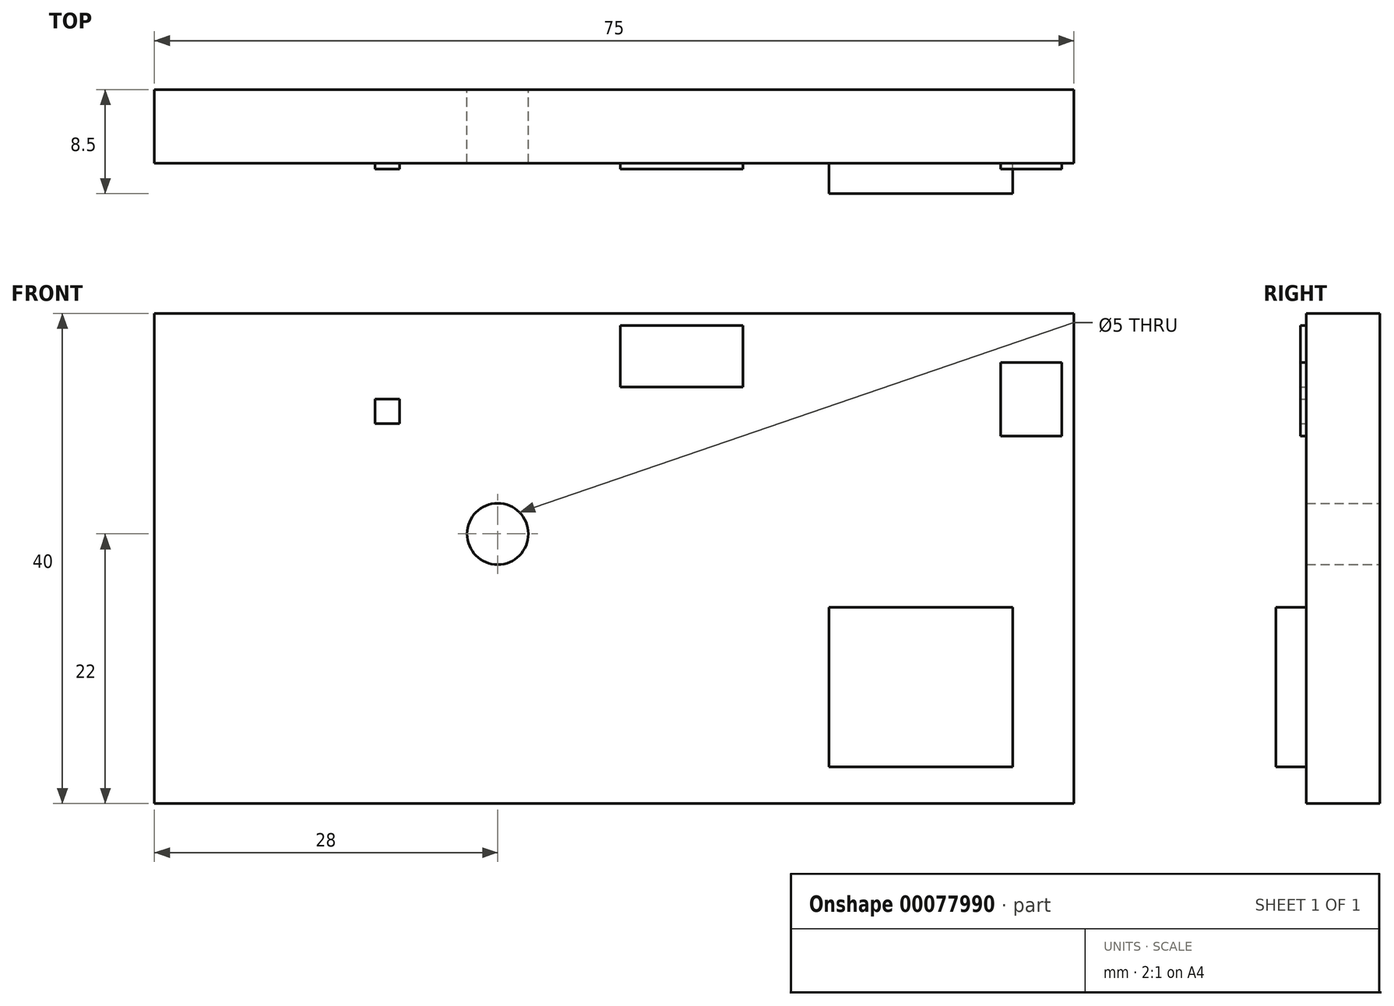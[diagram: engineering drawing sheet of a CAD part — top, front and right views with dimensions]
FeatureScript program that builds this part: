
annotation { "Feature Type Name" : "Feature", "Feature Type Description" : "" }
export const myFeature = defineFeature(function(context is Context, id is Id, definition is map)
    precondition{}
    {
        {
            var Q0;
            Q0=qCreatedBy(makeId("Front.planeOp"),FACE);
            var sketch = newSketch(context, id + "F0", { "sketchPlane" : qUnion([Q0])});
            skLineSegment(sketch, "E0", {"start": v(37.5, -20) * mm, "end": v(-37.5, -20) * mm});
            skLineSegment(sketch, "E1", {"start": v(-37.5, -20) * mm, "end": v(-37.5, 20) * mm});
            skLineSegment(sketch, "E2", {"start": v(-37.5, 20) * mm, "end": v(37.5, 20) * mm});
            skLineSegment(sketch, "E3", {"start": v(37.5, 20) * mm, "end": v(37.5, -20) * mm});
            skPoint(sketch, "E4.endSnap0", {"position": v(-37.5, 0) * mm});
            skCircle(sketch, "E5", {"center": v(-9.5, 2) * mm, "radius": 2.5 * mm});
            skSolve(sketch);
        }
        {
            var Q0;
            Q0=qSketchRegion(id+"F0",true);
            extrude(context, id + "F1", {"entities" : qUnion([Q0]), "depth" : 6 * mm});
        }
        {
            var Q0;
            Q0=makeQuery(id+"F1.opExtrude","CAP_FACE",FACE,{"disambiguationData":[OSD([sQuery(id+"F0.wireOp",EDGE,"E0"),sQuery(id+"F0.wireOp",EDGE,"E1"),sQuery(id+"F0.wireOp",EDGE,"E2"),sQuery(id+"F0.wireOp",EDGE,"E3")])],"isStart":false});
            var sketch = newSketch(context, id + "F2", { "sketchPlane" : qUnion([Q0])});
            skLineSegment(sketch, "E6", {"start": v(0.5, 19) * mm, "end": v(0.5, 14) * mm});
            skLineSegment(sketch, "E7", {"start": v(36.5, 16) * mm, "end": v(31.5, 16) * mm});
            skLineSegment(sketch, "E8", {"start": v(0.5, 14) * mm, "end": v(10.5, 14) * mm});
            skLineSegment(sketch, "E9", {"start": v(10.5, 14) * mm, "end": v(10.5, 19) * mm});
            skLineSegment(sketch, "E10", {"start": v(10.5, 19) * mm, "end": v(0.5, 19) * mm});
            skLineSegment(sketch, "E11", {"start": v(31.5, 16) * mm, "end": v(31.5, 10) * mm});
            skLineSegment(sketch, "E12", {"start": v(31.5, 10) * mm, "end": v(36.5, 10) * mm});
            skLineSegment(sketch, "E13", {"start": v(36.5, 10) * mm, "end": v(36.5, 16) * mm});
            skLineSegment(sketch, "E14", {"start": v(-17.5, 13) * mm, "end": v(-17.5, 11) * mm});
            skLineSegment(sketch, "E15", {"start": v(-17.5, 11) * mm, "end": v(-19.5, 11) * mm});
            skLineSegment(sketch, "E16", {"start": v(-19.5, 11) * mm, "end": v(-19.5, 13) * mm});
            skLineSegment(sketch, "E17", {"start": v(-19.5, 13) * mm, "end": v(-17.5, 13) * mm});
            skSolve(sketch);
        }
        {
            var Q0;
            Q0=qSketchRegion(id+"F2",true);
            extrude(context, id + "F3", {"entities" : qUnion([Q0]), "operationType" : NewBodyOperationType.ADD, "depth" : 0.5 * mm});
        }
        {
            var Q0;
            Q0=makeQuery(id+"F1.opExtrude","CAP_FACE",FACE,{"disambiguationData":[OSD([sQuery(id+"F0.wireOp",EDGE,"E0"),sQuery(id+"F0.wireOp",EDGE,"E1"),sQuery(id+"F0.wireOp",EDGE,"E2"),sQuery(id+"F0.wireOp",EDGE,"E3")])],"isStart":false});
            var sketch = newSketch(context, id + "F4", { "sketchPlane" : qUnion([Q0])});
            skLineSegment(sketch, "E18", {"start": v(17.5, -17) * mm, "end": v(17.5, -4) * mm});
            skLineSegment(sketch, "E19", {"start": v(17.5, -4) * mm, "end": v(32.5, -4) * mm});
            skLineSegment(sketch, "E20", {"start": v(32.5, -4) * mm, "end": v(32.5, -17) * mm});
            skLineSegment(sketch, "E21", {"start": v(32.5, -17) * mm, "end": v(17.5, -17) * mm});
            skSolve(sketch);
        }
        {
            var Q0;
            Q0=qSketchRegion(id+"F4",true);
            extrude(context, id + "F5", {"entities" : qUnion([Q0]), "operationType" : NewBodyOperationType.ADD, "depth" : 2.5 * mm});
        }
    });
